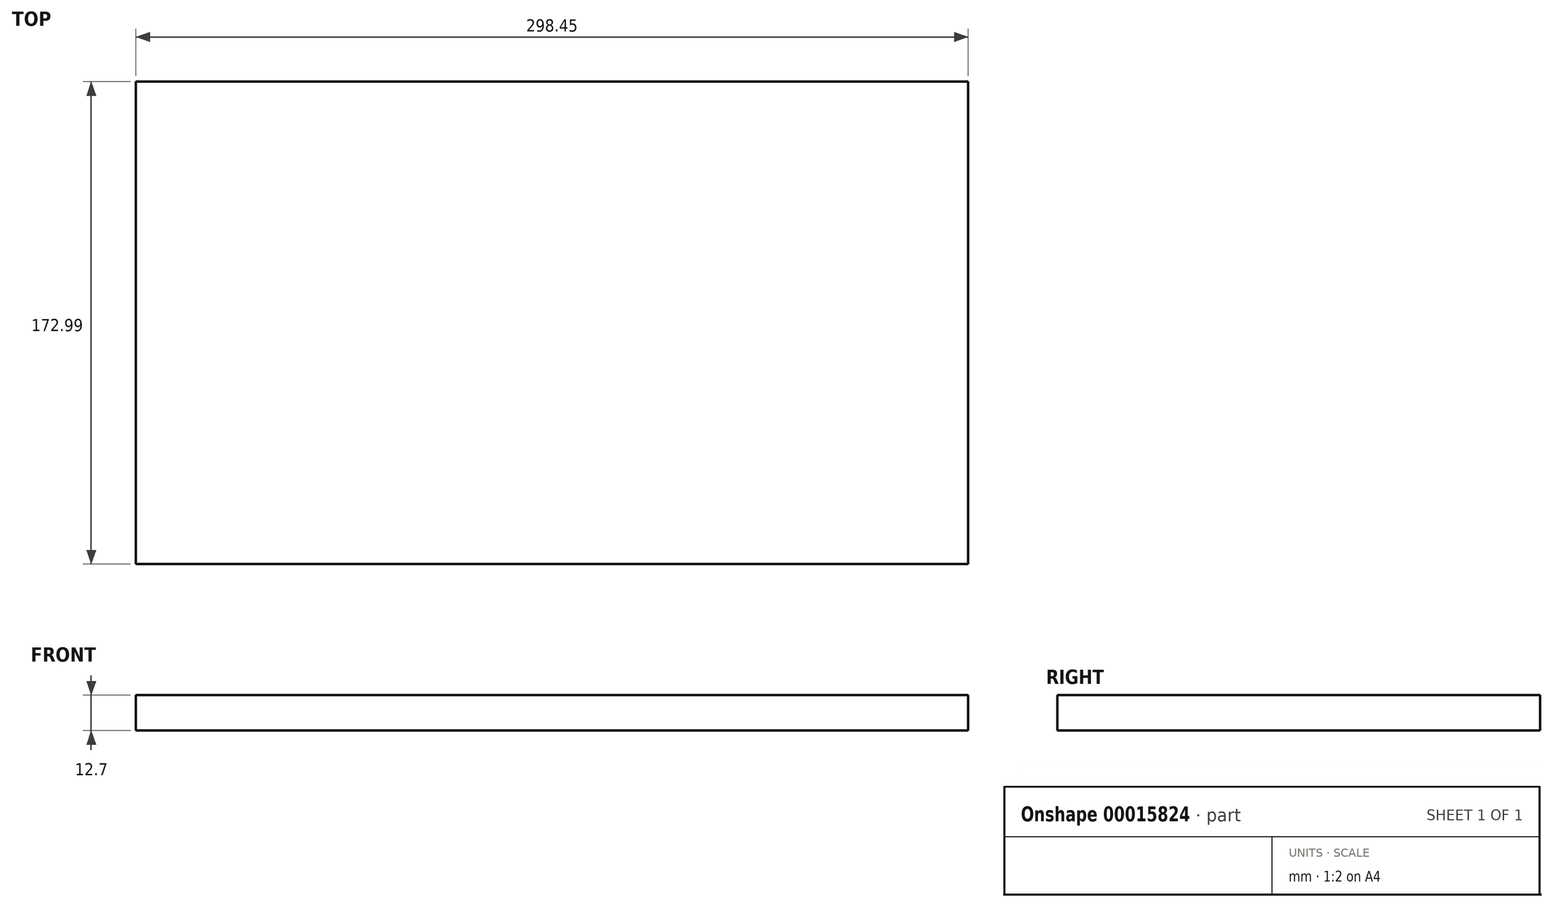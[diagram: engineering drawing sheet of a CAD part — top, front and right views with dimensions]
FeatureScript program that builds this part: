
annotation { "Feature Type Name" : "Feature", "Feature Type Description" : "" }
export const myFeature = defineFeature(function(context is Context, id is Id, definition is map)
    precondition{}
    {
        {
            var Q0;
            Q0=qCreatedBy(makeId("Top.planeOp"),FACE);
            var sketch = newSketch(context, id + "F0", { "sketchPlane" : qUnion([Q0])});
            skLineSegment(sketch, "E0.bottom", {"start": v(0, 0) * mm, "end": v(298.45, 0) * mm});
            skLineSegment(sketch, "E0.top", {"start": v(0, -173) * mm, "end": v(298.45, -173) * mm});
            skLineSegment(sketch, "E0.left", {"start": v(0, 0) * mm, "end": v(0, -173) * mm});
            skLineSegment(sketch, "E0.right", {"start": v(298.45, 0) * mm, "end": v(298.45, -173) * mm});
            skSolve(sketch);
        }
        {
            var Q0;
            Q0=qSketchRegion(id+"F0",true);
            extrude(context, id + "F1", {"entities" : qUnion([Q0]), "depth" : 12.7 * mm});
        }
    });
